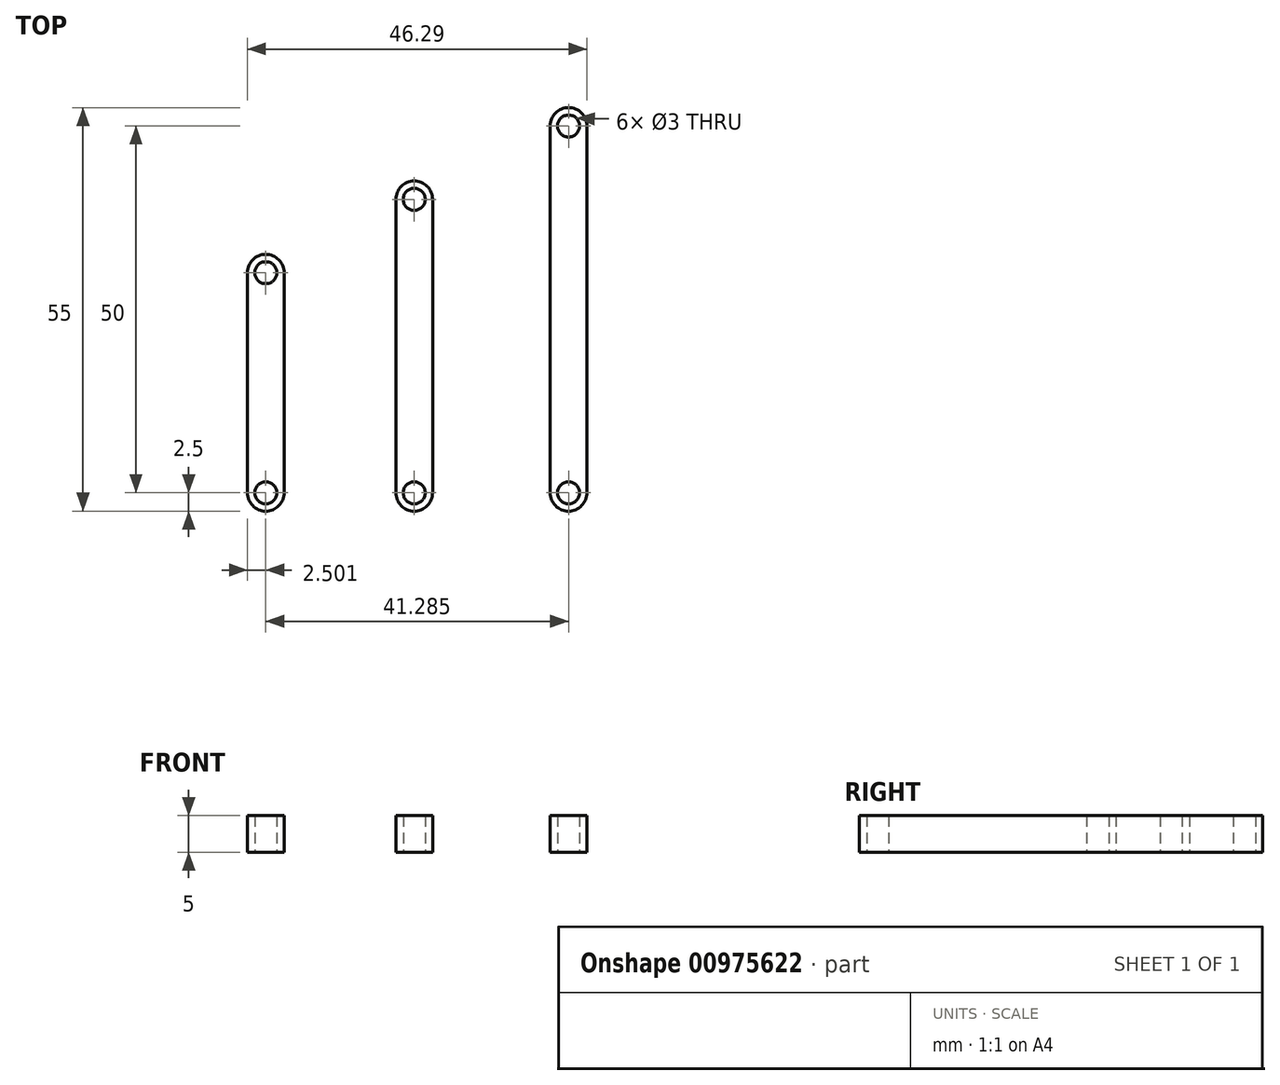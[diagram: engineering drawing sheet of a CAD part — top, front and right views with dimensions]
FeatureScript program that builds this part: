
annotation { "Feature Type Name" : "Feature", "Feature Type Description" : "" }
export const myFeature = defineFeature(function(context is Context, id is Id, definition is map)
    precondition{}
    {
        {
            var Q0;
            Q0=qCreatedBy(makeId("Top.planeOp"), FACE);
            var sketch = newSketch(context, id + "F0", { "sketchPlane" : qUnion([Q0])});
            skLineSegment(sketch, "E0", {"start": v(-11.67, 23.13) * mm, "end": v(-11.67, 73.13) * mm, "construction": true});
            skLineSegment(sketch, "E1", {"start": v(-32.72, 23.13) * mm, "end": v(-32.72, 63.13) * mm, "construction": true});
            skLineSegment(sketch, "E2", {"start": v(-52.96, 23.13) * mm, "end": v(-52.96, 53.13) * mm, "construction": true});
            skArc(sketch, "E3.0.startCap", {"start": v(-9.17, 23.13) * mm, "mid": v(-11.67, 20.63) * mm, "end": v(-14.17, 23.13) * mm});
            skArc(sketch, "E3.0.endCap", {"start": v(-14.17, 73.13) * mm, "mid": v(-11.67, 75.63) * mm, "end": v(-9.17, 73.13) * mm});
            skLineSegment(sketch, "E3.0.left", {"start": v(-14.17, 23.13) * mm, "end": v(-14.17, 73.13) * mm});
            skLineSegment(sketch, "E3.0.right", {"start": v(-9.17, 23.13) * mm, "end": v(-9.17, 73.13) * mm});
            skArc(sketch, "E4.0.startCap", {"start": v(-50.46, 23.13) * mm, "mid": v(-52.96, 20.63) * mm, "end": v(-55.46, 23.13) * mm});
            skArc(sketch, "E4.0.endCap", {"start": v(-55.46, 53.13) * mm, "mid": v(-52.96, 55.63) * mm, "end": v(-50.46, 53.13) * mm});
            skLineSegment(sketch, "E4.0.left", {"start": v(-55.46, 23.13) * mm, "end": v(-55.46, 53.13) * mm});
            skLineSegment(sketch, "E4.0.right", {"start": v(-50.46, 23.13) * mm, "end": v(-50.46, 53.13) * mm});
            skArc(sketch, "E4.1.startCap", {"start": v(-30.22, 23.13) * mm, "mid": v(-32.72, 20.63) * mm, "end": v(-35.22, 23.13) * mm});
            skArc(sketch, "E4.1.endCap", {"start": v(-35.22, 63.13) * mm, "mid": v(-32.72, 65.63) * mm, "end": v(-30.22, 63.13) * mm});
            skLineSegment(sketch, "E4.1.left", {"start": v(-35.22, 23.13) * mm, "end": v(-35.22, 63.13) * mm});
            skLineSegment(sketch, "E4.1.right", {"start": v(-30.22, 23.13) * mm, "end": v(-30.22, 63.13) * mm});
            skCircle(sketch, "E5", {"center": v(-52.96, 53.13) * mm, "radius": 1.5 * mm});
            skCircle(sketch, "E6", {"center": v(-32.72, 63.13) * mm, "radius": 1.5 * mm});
            skCircle(sketch, "E7", {"center": v(-11.67, 73.13) * mm, "radius": 1.5 * mm});
            skCircle(sketch, "E8", {"center": v(-11.67, 23.13) * mm, "radius": 1.5 * mm});
            skCircle(sketch, "E9", {"center": v(-32.72, 23.13) * mm, "radius": 1.5 * mm});
            skCircle(sketch, "E10", {"center": v(-52.96, 23.13) * mm, "radius": 1.5 * mm});
            skSolve(sketch);
        }
        {
            var Q0;
            Q0 = qSketchRegion(id + "F0", true);
            extrude(context, id + "F1", {"entities" : qUnion([Q0]), "domain" : OperationDomain.MODEL, "flatOperationType" : FlatOperationType.REMOVE, "depth" : 5 * mm, "offsetDistance" : 25 * mm});
        }
    });
